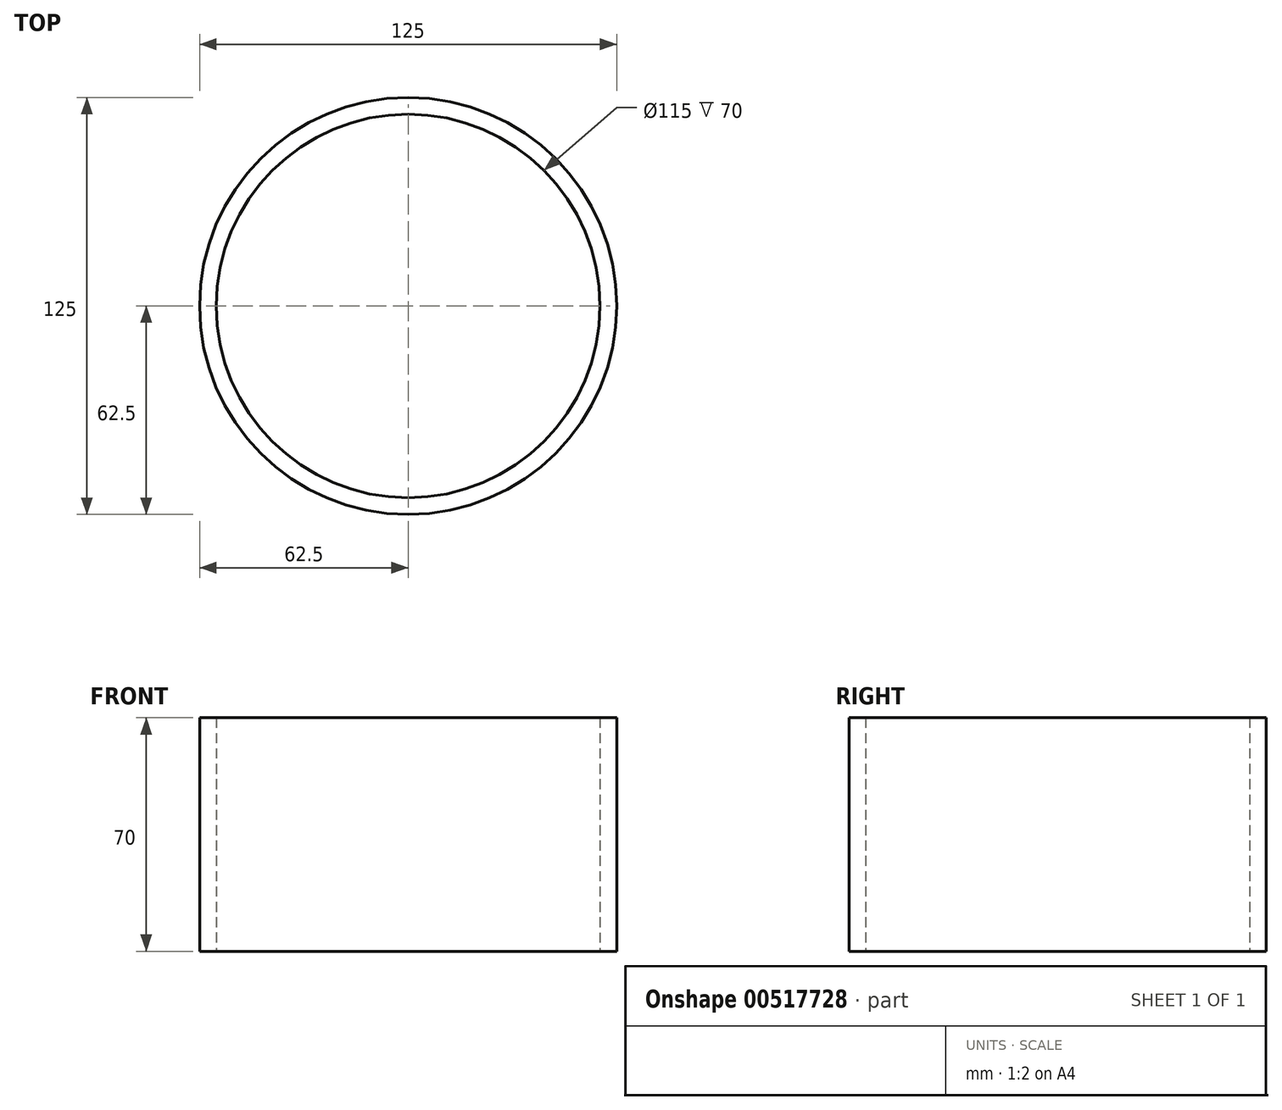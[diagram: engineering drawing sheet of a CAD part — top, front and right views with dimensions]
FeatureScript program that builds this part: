
annotation { "Feature Type Name" : "Feature", "Feature Type Description" : "" }
export const myFeature = defineFeature(function(context is Context, id is Id, definition is map)
    precondition{}
    {
        {
            var Q0;
            Q0=qCreatedBy(makeId("Top.planeOp"),FACE);
            var sketch = newSketch(context, id + "F0", { "sketchPlane" : qUnion([Q0])});
            skCircle(sketch, "E0", {"center": v(0, 0) * mm, "radius": 62.5 * mm});
            skCircle(sketch, "E1.0", {"center": v(0, 0) * mm, "radius": 57.5 * mm});
            skSolve(sketch);
        }
        {
            var Q0;
            Q0=makeQuery(id+"F0.imprint","IMPRINT",FACE,{"disambiguationData":[TD([[makeQuery(id+"F0.imprint","IMPRINT",EDGE,{"derivedFrom":sQuery(id+"F0.wireOp",EDGE,"E0")}),1.0]])]});
            extrude(context, id + "F1", {"entities" : qUnion([Q0]), "depth" : 70 * mm, "offsetDistance" : 25 * mm});
        }
    });
